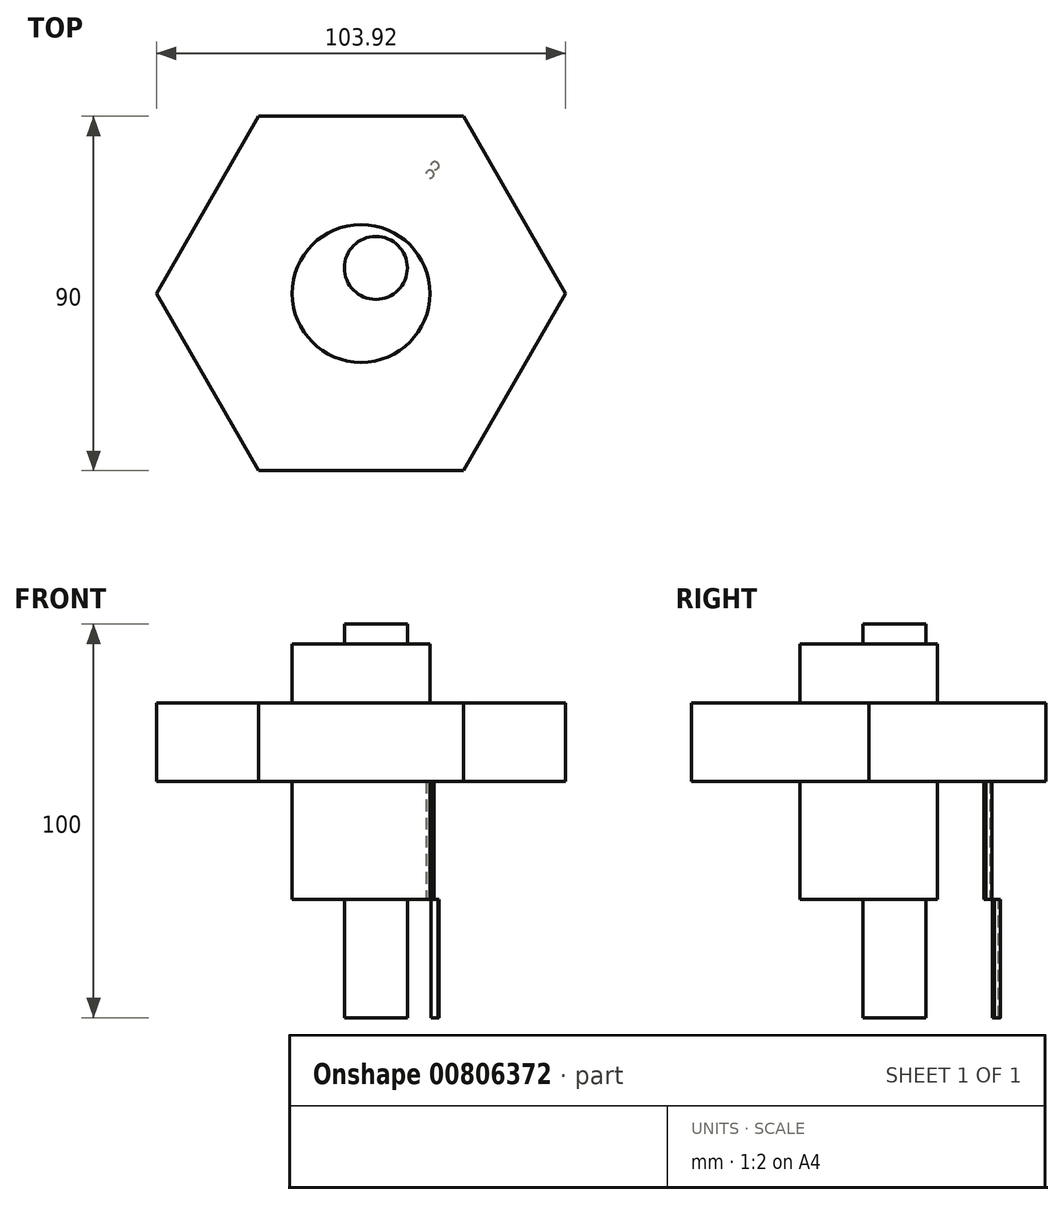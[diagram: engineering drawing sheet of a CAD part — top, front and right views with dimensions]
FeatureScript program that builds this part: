
annotation { "Feature Type Name" : "Feature", "Feature Type Description" : "" }
export const myFeature = defineFeature(function(context is Context, id is Id, definition is map)
    precondition{}
    {
        {
            var Q0;
            Q0=qCreatedBy(makeId("Top.planeOp"),FACE);
            var sketch = newSketch(context, id + "F0", { "sketchPlane" : qUnion([Q0])});
            skCircle(sketch, "E0", {"center": v(0, 0) * mm, "radius": 37.5 * mm, "construction": true});
            skCircle(sketch, "E1", {"center": v(0, 0) * mm, "radius": 7.5 * mm});
            skLineSegment(sketch, "E2", {"start": v(0, 0) * mm, "end": v(3.75, 6.5) * mm});
            skLineSegment(sketch, "E3", {"start": v(0, 0) * mm, "end": v(-45.1, 0) * mm, "construction": true});
            skCircle(sketch, "E4", {"center": v(3.75, 6.5) * mm, "radius": 8 * mm});
            skCircle(sketch, "E5", {"center": v(3.75, 6.5) * mm, "radius": 27.5 * mm});
            skCircle(sketch, "E6", {"center": v(0, 0) * mm, "radius": 35 * mm});
            skCircle(sketch, "E7", {"center": v(0, 0) * mm, "radius": 17.5 * mm});
            skCircle(sketch, "E8.cCircle", {"center": v(0, 0) * mm, "radius": 45 * mm, "construction": true});
            skLineSegment(sketch, "E8.0", {"start": v(-25.98, 45) * mm, "end": v(25.98, 45) * mm});
            skLineSegment(sketch, "E8.1", {"start": v(25.98, 45) * mm, "end": v(51.96, 0) * mm});
            skLineSegment(sketch, "E8.2", {"start": v(51.96, 0) * mm, "end": v(25.98, -45) * mm});
            skLineSegment(sketch, "E8.3", {"start": v(25.98, -45) * mm, "end": v(-25.98, -45) * mm});
            skLineSegment(sketch, "E8.4", {"start": v(-25.98, -45) * mm, "end": v(-51.96, 0) * mm});
            skLineSegment(sketch, "E8.5", {"start": v(-51.96, 0) * mm, "end": v(-25.98, 45) * mm});
            skPoint(sketch, "E8.0.midPoint", {"position": v(0, 45) * mm});
            skLineSegment(sketch, "E9", {"start": v(3.75, 6.5) * mm, "end": v(17.5, 30.31) * mm, "construction": true});
            skCircle(sketch, "E10", {"center": v(17.5, 30.31) * mm, "radius": 1 * mm, "construction": true});
            skLineSegment(sketch, "E11", {"start": v(3.75, 6.5) * mm, "end": v(18.75, 32.48) * mm, "construction": true});
            skCircle(sketch, "E12", {"center": v(18.75, 32.48) * mm, "radius": 1 * mm, "construction": true});
            skSolve(sketch);
        }
        {
            var Q0;
            Q0=makeQuery(id+"F0.imprint","IMPRINT",FACE,{"disambiguationData":[TD([[makeQuery(id+"F0.imprint","IMPRINT",EDGE,{"derivedFrom":sQuery(id+"F0.wireOp",EDGE,"E6")}),-1.0]])]});
            extrude(context, id + "F1", {"entities" : qUnion([Q0]), "depth" : 30 * mm, "offsetDistance" : 25 * mm});
        }
        {
            var Q0;
            Q0=makeQuery(id+"F1.opExtrude","CAP_FACE",FACE,{"disambiguationData":[OSD([sQuery(id+"F0.wireOp",EDGE,"E6"),sQuery(id+"F0.wireOp",EDGE,"E8.0"),sQuery(id+"F0.wireOp",EDGE,"E8.1"),sQuery(id+"F0.wireOp",EDGE,"E8.2"),sQuery(id+"F0.wireOp",EDGE,"E8.3"),sQuery(id+"F0.wireOp",EDGE,"E8.4"),sQuery(id+"F0.wireOp",EDGE,"E8.5")])],"isStart":false});
            var sketch = newSketch(context, id + "F2", { "sketchPlane" : qUnion([Q0])});
            skLineSegment(sketch, "E13.0", {"start": v(-51.96, 0) * mm, "end": v(-25.98, 45) * mm});
            skLineSegment(sketch, "E14.0", {"start": v(-25.98, 45) * mm, "end": v(25.98, 45) * mm});
            skLineSegment(sketch, "E15.0", {"start": v(25.98, 45) * mm, "end": v(51.96, 0) * mm});
            skLineSegment(sketch, "E16.0", {"start": v(51.96, 0) * mm, "end": v(25.98, -45) * mm});
            skLineSegment(sketch, "E17.0", {"start": v(25.98, -45) * mm, "end": v(-25.98, -45) * mm});
            skLineSegment(sketch, "E18.0", {"start": v(-25.98, -45) * mm, "end": v(-51.96, 0) * mm});
            skCircle(sketch, "E19.0", {"center": v(0, 0) * mm, "radius": 17.5 * mm});
            skSolve(sketch);
        }
        {
            var Q0;
            Q0 = qSketchRegion(id + "F2", true);
            extrude(context, id + "F3", {"entities" : qUnion([Q0]), "operationType" : NewBodyOperationType.ADD, "depth" : 20 * mm, "offsetDistance" : 25 * mm});
        }
        {
            var Q0;
            {var subQ0=sQuery(id+"F0.wireOp",EDGE,"E1");var subQ1=makeQuery(id+"F0.imprint","IMPRINT",VERTEX,{"derivedFrom":subQ0});Q0=makeQuery(id+"F0.imprint","IMPRINT",FACE,{"disambiguationData":[TD([[makeQuery(id+"F0.imprint","IMPRINT",EDGE,{"disambiguationData":[TD([[subQ1,-1.0]])],"derivedFrom":subQ0}),-1.0]])]});}
            var Q1;
            {var subQ0=sQuery(id+"F0.wireOp",EDGE,"E1");var subQ1=makeQuery(id+"F0.imprint","IMPRINT",VERTEX,{"derivedFrom":subQ0});Q1=makeQuery(id+"F0.imprint","IMPRINT",FACE,{"disambiguationData":[TD([[makeQuery(id+"F0.imprint","IMPRINT",EDGE,{"disambiguationData":[TD([[subQ1,-1.0]])],"derivedFrom":subQ0}),1.0]])]});}
            extrude(context, id + "F4", {"entities" : qUnion([Q0, Q1]), "depth" : 30 * mm, "offsetDistance" : 25 * mm});
        }
        {
            var Q0;
            Q0=makeQuery(id+"F4.opExtrude","CAP_FACE",FACE,{"disambiguationData":[OSD([sQuery(id+"F0.wireOp",EDGE,"E4")])],"isStart":false});
            var sketch = newSketch(context, id + "F5", { "sketchPlane" : qUnion([Q0])});
            skCircle(sketch, "E20.0", {"center": v(0, 0) * mm, "radius": 17.5 * mm});
            skSolve(sketch);
        }
        {
            var Q0;
            Q0=makeQuery(id+"F5.imprint","IMPRINT",FACE,{"disambiguationData":[TD([[makeQuery(id+"F5.imprint","IMPRINT",EDGE,{"derivedFrom":sQuery(id+"F5.wireOp",EDGE,"E20.0")}),1.0]])]});
            var Q1;
            Q1=makeQuery(id+"F5.imprint","IMPRINT",FACE,{"disambiguationData":[TD([[makeQuery(id+"F5.imprint","IMPRINT",EDGE,{"derivedFrom":makeQuery(id+"F4.opExtrude","CAP_EDGE",EDGE,{"disambiguationData":[OSD([sQuery(id+"F0.wireOp",EDGE,"E4")])],"isStart":false})}),1.0]])]});
            extrude(context, id + "F6", {"entities" : qUnion([Q0, Q1]), "operationType" : NewBodyOperationType.ADD, "depth" : 35 * mm, "offsetDistance" : 25 * mm});
        }
        {
            var Q0;
            Q0=makeQuery(id+"F0.imprint","IMPRINT",FACE,{"disambiguationData":[TD([[makeQuery(id+"F0.imprint","IMPRINT",EDGE,{"derivedFrom":sQuery(id+"F0.wireOp",EDGE,"E5")}),1.0]])]});
            var Q1;
            Q1=makeQuery(id+"F0.imprint","IMPRINT",FACE,{"disambiguationData":[TD([[makeQuery(id+"F0.imprint","IMPRINT",EDGE,{"derivedFrom":sQuery(id+"F0.wireOp",EDGE,"E7")}),1.0]])]});
            var Q2;
            {var subQ0=sQuery(id+"F0.wireOp",EDGE,"E4");var subQ1=sQuery(id+"F0.wireOp",EDGE,"E1");var subQ2=makeQuery(id+"F0.imprint","INTERSECT",VERTEX,{"disambiguationData":[OD(0.0)],"derivedFrom":[subQ1,subQ0]});Q2=makeQuery(id+"F0.imprint","IMPRINT",FACE,{"disambiguationData":[TD([[makeQuery(id+"F0.imprint","IMPRINT",EDGE,{"disambiguationData":[TD([[subQ2,-1.0]])],"derivedFrom":subQ1}),1.0]])]});}
            extrude(context, id + "F7", {"entities" : qUnion([Q0, Q1, Q2]), "depth" : 30 * mm, "offsetDistance" : 25 * mm});
        }
        {
            var Q0;
            {var subQ0=sQuery(id+"F0.wireOp",EDGE,"E1");var subQ1=makeQuery(id+"F0.imprint","IMPRINT",VERTEX,{"derivedFrom":subQ0});Q0=makeQuery(id+"F0.imprint","IMPRINT",FACE,{"disambiguationData":[TD([[makeQuery(id+"F0.imprint","IMPRINT",EDGE,{"disambiguationData":[TD([[subQ1,-1.0]])],"derivedFrom":subQ0}),-1.0]])]});}
            var sketch = newSketch(context, id + "F8", { "sketchPlane" : qUnion([Q0])});
            skCircle(sketch, "E21.0", {"center": v(3.75, 6.5) * mm, "radius": 8 * mm});
            skSolve(sketch);
        }
        {
            var Q0;
            {var subQ1=sQuery(id+"F0.wireOp",EDGE,"E1");var subQ2=makeQuery(id+"F0.imprint","IMPRINT",VERTEX,{"derivedFrom":subQ1});var subQ4=makeQuery(id+"F0.imprint","IMPRINT",EDGE,{"disambiguationData":[TD([[subQ2,-1.0]])],"derivedFrom":subQ1});Q0=makeQuery(id+"F8.imprint","IMPRINT",FACE,{"disambiguationData":[TD([[makeQuery(id+"F8.imprint","IMPRINT",EDGE,{"derivedFrom":subQ4}),1.0]])]});}
            var Q1;
            {var subQ1=sQuery(id+"F0.wireOp",EDGE,"E1");var subQ2=makeQuery(id+"F0.imprint","IMPRINT",VERTEX,{"derivedFrom":subQ1});var subQ4=makeQuery(id+"F0.imprint","IMPRINT",EDGE,{"disambiguationData":[TD([[subQ2,-1.0]])],"derivedFrom":subQ1});Q1=makeQuery(id+"F8.imprint","IMPRINT",FACE,{"disambiguationData":[TD([[makeQuery(id+"F8.imprint","IMPRINT",EDGE,{"derivedFrom":subQ4}),-1.0]])]});}
            extrude(context, id + "F9", {"entities" : qUnion([Q0, Q1]), "operationType" : NewBodyOperationType.ADD, "oppositeDirection" : true, "depth" : 30 * mm, "offsetDistance" : 25 * mm});
        }
        {
            var Q0;
            Q0=makeQuery(id+"F6.opExtrude","CAP_FACE",FACE,{"disambiguationData":[OSD([sQuery(id+"F5.wireOp",EDGE,"E20.0")])],"isStart":false});
            var sketch = newSketch(context, id + "F10", { "sketchPlane" : qUnion([Q0])});
            skCircle(sketch, "E22.0", {"center": v(3.75, 6.5) * mm, "radius": 8 * mm});
            skSolve(sketch);
        }
        {
            var Q0;
            Q0=makeQuery(id+"F10.imprint","IMPRINT",FACE,{"disambiguationData":[TD([[makeQuery(id+"F10.imprint","IMPRINT",EDGE,{"derivedFrom":sQuery(id+"F10.wireOp",EDGE,"E22.0")}),1.0]])]});
            extrude(context, id + "F11", {"entities" : qUnion([Q0]), "operationType" : NewBodyOperationType.ADD, "depth" : 5 * mm, "offsetDistance" : 25 * mm});
        }
        {
            var Q0;
            Q0=qCreatedBy(makeId("Top.planeOp"),FACE);
            var sketch = newSketch(context, id + "F12", { "sketchPlane" : qUnion([Q0])});
            skCircle(sketch, "E23.0", {"center": v(0, 0) * mm, "radius": 37.5 * mm});
            skCircle(sketch, "E24.0", {"center": v(3.75, 6.5) * mm, "radius": 8 * mm});
            skCircle(sketch, "E25", {"center": v(3.75, 6.5) * mm, "radius": 30 * mm});
            skCircle(sketch, "E26.cCircle", {"center": v(0, -0.57) * mm, "radius": 50 * mm, "construction": true});
            skLineSegment(sketch, "E26.0", {"start": v(20.71, 49.43) * mm, "end": v(50, 20.14) * mm});
            skLineSegment(sketch, "E26.1", {"start": v(50, 20.14) * mm, "end": v(50, -21.28) * mm});
            skLineSegment(sketch, "E26.2", {"start": v(50, -21.28) * mm, "end": v(20.71, -50.57) * mm});
            skLineSegment(sketch, "E26.3", {"start": v(20.71, -50.57) * mm, "end": v(-20.71, -50.57) * mm});
            skLineSegment(sketch, "E26.4", {"start": v(-20.71, -50.57) * mm, "end": v(-50, -21.28) * mm});
            skLineSegment(sketch, "E26.5", {"start": v(-50, -21.28) * mm, "end": v(-50, 20.14) * mm});
            skLineSegment(sketch, "E26.6", {"start": v(-50, 20.14) * mm, "end": v(-20.71, 49.43) * mm});
            skLineSegment(sketch, "E26.7", {"start": v(-20.71, 49.43) * mm, "end": v(20.71, 49.43) * mm});
            skPoint(sketch, "E26.0.midPoint", {"position": v(35.36, 34.78) * mm});
            skSolve(sketch);
        }
        {
            var Q0;
            Q0=makeQuery(id+"F12.imprint","IMPRINT",FACE,{"disambiguationData":[TD([[makeQuery(id+"F12.imprint","IMPRINT",EDGE,{"derivedFrom":sQuery(id+"F12.wireOp",EDGE,"E23.0")}),-1.0]])]});
            extrude(context, id + "F13", {"entities" : qUnion([Q0]), "oppositeDirection" : true, "depth" : 30 * mm, "offsetDistance" : 25 * mm});
        }
        {
            var Q0;
            Q0=makeQuery(id+"F12.imprint","IMPRINT",FACE,{"disambiguationData":[TD([[makeQuery(id+"F12.imprint","IMPRINT",EDGE,{"derivedFrom":sQuery(id+"F12.wireOp",EDGE,"E24.0")}),-1.0]])]});
            var sketch = newSketch(context, id + "F14", { "sketchPlane" : qUnion([Q0])});
            skCircle(sketch, "E27.0", {"center": v(3.75, 6.5) * mm, "radius": 30 * mm});
            skCircle(sketch, "E28.0", {"center": v(3.75, 6.5) * mm, "radius": 8 * mm});
            skSolve(sketch);
        }
        {
            var Q0;
            Q0=makeQuery(id+"F14.imprint","IMPRINT",FACE,{"disambiguationData":[TD([[makeQuery(id+"F14.imprint","IMPRINT",EDGE,{"derivedFrom":sQuery(id+"F14.wireOp",EDGE,"E27.0")}),1.0]])]});
            extrude(context, id + "F15", {"entities" : qUnion([Q0]), "operationType" : NewBodyOperationType.ADD, "oppositeDirection" : true, "depth" : 30 * mm, "offsetDistance" : 25 * mm});
        }
        {
            var Q0;
            Q0=qCreatedBy(makeId("Top.planeOp"),FACE);
            var sketch = newSketch(context, id + "F16", { "sketchPlane" : qUnion([Q0])});
            skCircle(sketch, "E29.0", {"center": v(18.75, 32.48) * mm, "radius": 1 * mm});
            skCircle(sketch, "E30.0", {"center": v(17.5, 30.31) * mm, "radius": 1 * mm});
            skSolve(sketch);
        }
        {
            var Q0;
            Q0=makeQuery(id+"F16.imprint","IMPRINT",FACE,{"disambiguationData":[TD([[makeQuery(id+"F16.imprint","IMPRINT",EDGE,{"derivedFrom":sQuery(id+"F16.wireOp",EDGE,"E30.0")}),1.0]])]});
            extrude(context, id + "F17", {"entities" : qUnion([Q0]), "depth" : 30 * mm, "offsetDistance" : 25 * mm});
        }
        {
            var Q0;
            Q0=makeQuery(id+"F16.imprint","IMPRINT",FACE,{"disambiguationData":[TD([[makeQuery(id+"F16.imprint","IMPRINT",EDGE,{"derivedFrom":sQuery(id+"F16.wireOp",EDGE,"E29.0")}),1.0]])]});
            extrude(context, id + "F18", {"entities" : qUnion([Q0]), "oppositeDirection" : true, "depth" : 30 * mm, "offsetDistance" : 25 * mm});
        }
        {
            var Q0;
            Q0=makeQuery(id+"F17.opExtrude","SWEPT_BODY",BODY,{"disambiguationData":[OSD([sQuery(id+"F16.wireOp",EDGE,"E30.0")])]});
            var Q1;
            Q1=makeQuery(id+"F1.opExtrude","SWEPT_BODY",BODY,{"disambiguationData":[OSD([sQuery(id+"F0.wireOp",EDGE,"E6"),sQuery(id+"F0.wireOp",EDGE,"E8.0"),sQuery(id+"F0.wireOp",EDGE,"E8.1"),sQuery(id+"F0.wireOp",EDGE,"E8.2"),sQuery(id+"F0.wireOp",EDGE,"E8.3"),sQuery(id+"F0.wireOp",EDGE,"E8.4"),sQuery(id+"F0.wireOp",EDGE,"E8.5")])]});
            var Q2;
            Q2=makeQuery(id+"F7.opExtrude","SWEPT_BODY",BODY,{"disambiguationData":[OSD([sQuery(id+"F0.wireOp",EDGE,"E4"),sQuery(id+"F0.wireOp",EDGE,"E5")])]});
            booleanBodies(context, id + "F19", {"operationType" : BooleanOperationType.SUBTRACTION, "tools" : qUnion([Q0]), "targets" : qUnion([Q1, Q2]), "keepTools" : true});
        }
        {
            var Q0;
            Q0=makeQuery(id+"F18.opExtrude","SWEPT_BODY",BODY,{"disambiguationData":[OSD([sQuery(id+"F16.wireOp",EDGE,"E29.0")])]});
            var Q1;
            Q1=makeQuery(id+"F13.opExtrude","SWEPT_BODY",BODY,{"disambiguationData":[OSD([sQuery(id+"F12.wireOp",EDGE,"E23.0"),sQuery(id+"F12.wireOp",EDGE,"E26.0"),sQuery(id+"F12.wireOp",EDGE,"E26.1"),sQuery(id+"F12.wireOp",EDGE,"E26.2"),sQuery(id+"F12.wireOp",EDGE,"E26.3"),sQuery(id+"F12.wireOp",EDGE,"E26.4"),sQuery(id+"F12.wireOp",EDGE,"E26.5"),sQuery(id+"F12.wireOp",EDGE,"E26.6"),sQuery(id+"F12.wireOp",EDGE,"E26.7")])]});
            var Q2;
            Q2=makeQuery(id+"F7.opExtrude","SWEPT_BODY",BODY,{"disambiguationData":[OSD([sQuery(id+"F0.wireOp",EDGE,"E4"),sQuery(id+"F0.wireOp",EDGE,"E5")])]});
            booleanBodies(context, id + "F20", {"operationType" : BooleanOperationType.SUBTRACTION, "tools" : qUnion([Q0]), "targets" : qUnion([Q1, Q2]), "keepTools" : true});
        }
    });
